# Revit family: Zumtobel TECTON 2 Narrow Beam continuous row luminaire
name_source: partatom
category: Lighting Fixtures
units: mm (PartAtom-declared; Revit-internal decimal feet)

## family parameters
Cut with Voids When Loaded = Yes
Host = Face
Light Source = Yes
Maintain Annotation Orientation = No
Part Type = Normal
Room Calculation Point = Yes
Round Connector Dimension = Use Diameter
Shared = Yes

## types (13) — shared parameters
Assembly Code = Pr_70_70_48
Color Filter = 16777215
Colour = Colour
Description = Luminaires - lighting track and lighting accessories
Dimension = Dimension
Dimming Lamp Color Temperature Shift = <None>
Emit Shape Visible in Rendering = No
Emit from Rectangle Width = 59.26 mm
Export Type to IFC As = IfcLightFixtureType
Lamp = LED
Luminaire Height = 21.04 mm  [stored 0.0690289 ft]
Luminaire Width = 60 mm  [stored 0.19685 ft]
Manufacturer = Zumtobel Lighting
Tilt Angle = -90.00°
Type Housing Black = Zumtobel-Parts-TECTON 2-Continuous row luminaire-Housing : Black
Type Housing White = Zumtobel-Parts-TECTON 2-Continuous row luminaire-Housing : White
Type IFC Predefined Type = DIRECTIONSOURCE
URL = https://www.zumtobel.com
zero-valued in all types: Default Elevation

## per-type parameters (varying)
| type | Apparent Load | Black | Emit from Rectangle Length | L10 | L15 | L20 | L25 | Luminaire Length | Model | Photometric Web File | Power Factor | Type Housing | Type Image | White |
| TEC2 3k7-840 L10 NB LDE WH | 21 VA | No | 998 mm  [stored 3.27428 ft] | Yes | No | No | No | 1000 mm  [stored 3.28084 ft] | 42956147 | 42956147_(STD_LEO).IES | 0.98 | Zumtobel-Parts-TECTON 2-Continuous row luminaire-Housing : White | ZS_TE2_F_Batten_single_WH.jpg | Yes |
| TEC2 5k5-830 L15 NB LDE WH | 32 VA | No | 1498 mm  [stored 4.9147 ft] | No | Yes | No | No | 1500 mm  [stored 4.92126 ft] | 42956143 | 42956143_(STD_LEO).IES | 0.96 | Zumtobel-Parts-TECTON 2-Continuous row luminaire-Housing : White | ZS_TE2_F_Batten_single_WH.jpg | Yes |
| TEC2 5k5-840 L15 NB LDE WH | 31 VA | No | 1498 mm  [stored 4.9147 ft] | No | Yes | No | No | 1500 mm  [stored 4.92126 ft] | 42190984 | 42190984_(STD_LEO).IES | 0.96 | Zumtobel-Parts-TECTON 2-Continuous row luminaire-Housing : White | ZS_TE2_F_Batten_single_WH.jpg | Yes |
| TEC2 9k2-840 L25 NB LDE WH | 49 VA | No | 2498 mm  [stored 8.19554 ft] | No | No | No | Yes | 2500 mm  [stored 8.2021 ft] | 42190417 | 42190417_(STD_LEO).IES | 0.98 | Zumtobel-Parts-TECTON 2-Continuous row luminaire-Housing : White | ZS_TE2_F_Batten_single_WH.jpg | Yes |
| TEC2 11k-840 L20 NB LDE WH | 58 VA | No | 1998 mm  [stored 6.55512 ft] | No | No | Yes | No | 2000 mm  [stored 6.56168 ft] | 42190421 | 42190421_(STD_LEO).IES | 0.98 | Zumtobel-Parts-TECTON 2-Continuous row luminaire-Housing : White | ZS_TE2_F_Batten_single_WH.jpg | Yes |
| TEC2 8k-840 L15 NB LDE WH | 43 VA | No | 1498 mm  [stored 4.9147 ft] | No | Yes | No | No | 1500 mm  [stored 4.92126 ft] | 42190985 | 42190985_(STD_LEO).IES | 0.98 | Zumtobel-Parts-TECTON 2-Continuous row luminaire-Housing : White | ZS_TE2_F_Batten_single_WH.jpg | Yes |
| TEC2 12k-840 L15 NB LDE WH | 62 VA | No | 1498 mm  [stored 4.9147 ft] | No | Yes | No | No | 1500 mm  [stored 4.92126 ft] | 42955609 | 42955609_(STD_LEO).IES | 0.98 | Zumtobel-Parts-TECTON 2-Continuous row luminaire-Housing : White | ZS_TE2_F_Batten_single_WH.jpg | Yes |
| TEC2 16k-840 L20 NB LDE WH | 82 VA | No | 1998 mm  [stored 6.55512 ft] | No | No | Yes | No | 2000 mm  [stored 6.56168 ft] | 42190423 | 42190423_(STD_LEO).IES | 0.98 | Zumtobel-Parts-TECTON 2-Continuous row luminaire-Housing : White | ZS_TE2_F_Batten_single_WH.jpg | Yes |
| TEC2 20k-840 L25 NB LDE WH | 101 VA | No | 2498 mm  [stored 8.19554 ft] | No | No | No | Yes | 2500 mm  [stored 8.2021 ft] | 42190424 | 42190424_(STD_LEO).IES | 0.98 | Zumtobel-Parts-TECTON 2-Continuous row luminaire-Housing : White | ZS_TE2_F_Batten_single_WH.jpg | Yes |
| TEC2 3k7-830 L10 NB LDE BK | 21 VA | Yes | 998 mm  [stored 3.27428 ft] | Yes | No | No | No | 1000 mm  [stored 3.28084 ft] | 42956139 | 42956139_(STD_LEO).IES | 0.98 | Zumtobel-Parts-TECTON 2-Continuous row luminaire-Housing : Black | ZS_TE2_F_Batten_single_BK.jpg | No |
| TEC2 3k7-840 L10 NB LDE BK | 21 VA | Yes | 998 mm  [stored 3.27428 ft] | Yes | No | No | No | 1000 mm  [stored 3.28084 ft] | 42956180 | 42956180_(STD_LEO).IES | 0.98 | Zumtobel-Parts-TECTON 2-Continuous row luminaire-Housing : Black | ZS_TE2_F_Batten_single_BK.jpg | No |
| TEC2 5k5-830 L15 NB LDE BK | 32 VA | Yes | 1498 mm  [stored 4.9147 ft] | No | Yes | No | No | 1500 mm  [stored 4.92126 ft] | 42956144 | 42956144_(STD_LEO).IES | 0.96 | Zumtobel-Parts-TECTON 2-Continuous row luminaire-Housing : Black | ZS_TE2_F_Batten_single_BK.jpg | No |
| TEC2 7k3-830 L20 NB LDE BK | 41 VA | Yes | 1998 mm  [stored 6.55512 ft] | No | No | Yes | No | 2000 mm  [stored 6.56168 ft] | 42956149 | 42956149_(STD_LEO).IES | 0.98 | Zumtobel-Parts-TECTON 2-Continuous row luminaire-Housing : Black | ZS_TE2_F_Batten_single_BK.jpg | No |

note: [stored X ft] marks values corroborated as IEEE doubles in the binary element streams (Revit-internal decimal feet)

## geometry (parser evidence)
native form markers: Sweep x4
no freeform markers — native parametric forms only
